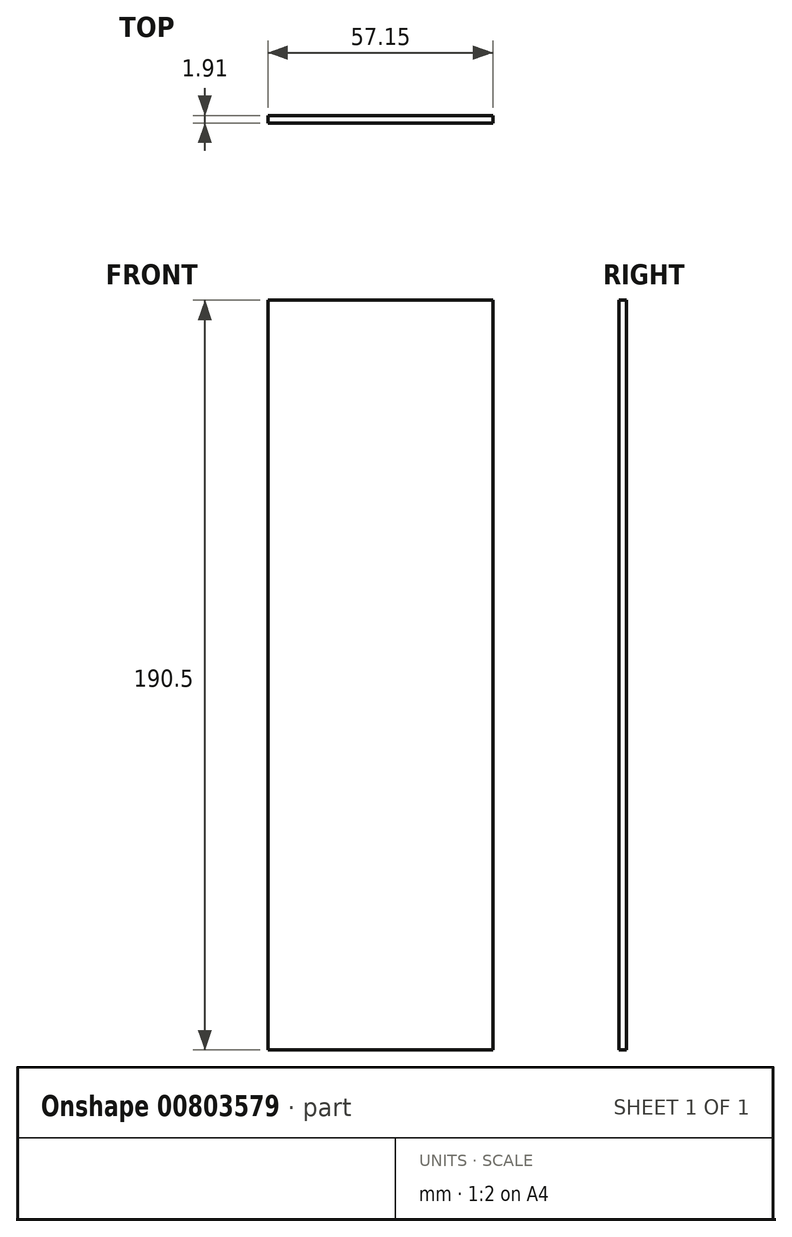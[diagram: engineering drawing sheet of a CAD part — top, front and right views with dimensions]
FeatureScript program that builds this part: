
annotation { "Feature Type Name" : "Feature", "Feature Type Description" : "" }
export const myFeature = defineFeature(function(context is Context, id is Id, definition is map)
    precondition{}
    {
        {
            var Q0;
            Q0=qCreatedBy(makeId("Front.planeOp"),FACE);
            var sketch = newSketch(context, id + "F0", { "sketchPlane" : qUnion([Q0])});
            skLineSegment(sketch, "E0.bottom", {"start": v(-150.4, 82.94) * mm, "end": v(-93.25, 82.94) * mm});
            skLineSegment(sketch, "E0.top", {"start": v(-150.4, -107.56) * mm, "end": v(-93.25, -107.56) * mm});
            skLineSegment(sketch, "E0.left", {"start": v(-150.4, 82.94) * mm, "end": v(-150.4, -107.56) * mm});
            skLineSegment(sketch, "E0.right", {"start": v(-93.25, 82.94) * mm, "end": v(-93.25, -107.56) * mm});
            skSolve(sketch);
        }
        {
            var Q0;
            Q0=makeQuery(id+"F0.imprint","IMPRINT",FACE,{"disambiguationData":[TD([[makeQuery(id+"F0.imprint","IMPRINT",EDGE,{"derivedFrom":sQuery(id+"F0.wireOp",EDGE,"E0.bottom")}),-1.0]])]});
            extrude(context, id + "F1", {"entities" : qUnion([Q0]), "depth" : 1.9 * mm, "offsetDistance" : 25.4 * mm});
        }
    });
